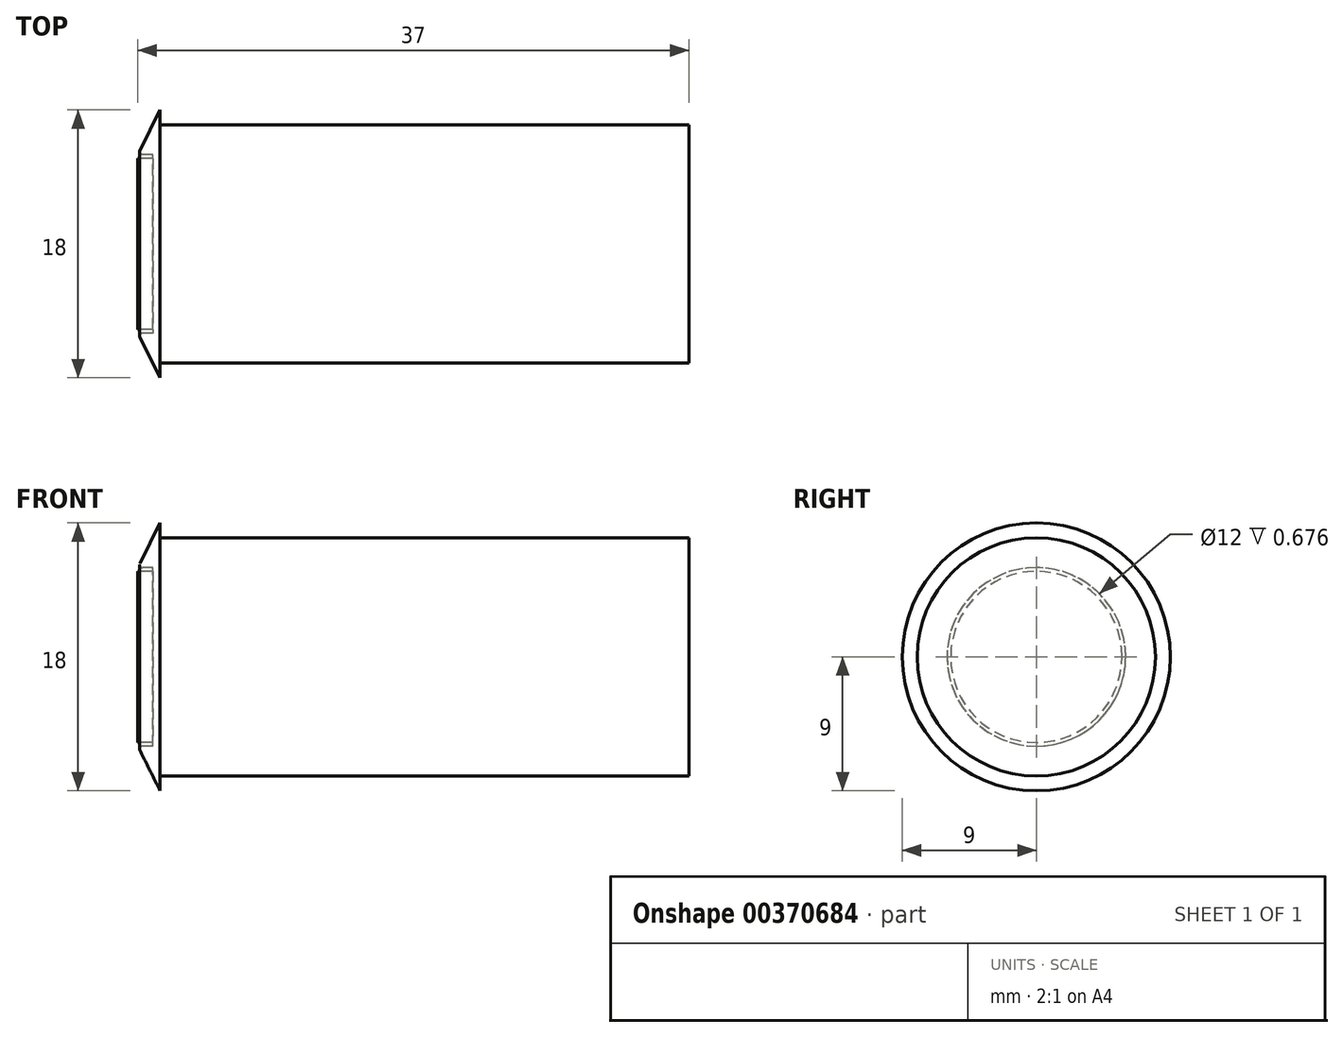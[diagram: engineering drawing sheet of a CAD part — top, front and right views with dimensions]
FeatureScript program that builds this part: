
annotation { "Feature Type Name" : "Feature", "Feature Type Description" : "" }
export const myFeature = defineFeature(function(context is Context, id is Id, definition is map)
    precondition{}
    {
        {
            var Q0;
            Q0=qCreatedBy(makeId("Front.planeOp"),FACE);
            var sketch = newSketch(context, id + "F0", { "sketchPlane" : qUnion([Q0])});
            skLineSegment(sketch, "E0", {"start": v(0, 0) * mm, "end": v(0, 6) * mm});
            skLineSegment(sketch, "E1", {"start": v(0, 6) * mm, "end": v(1.5, 9) * mm});
            skLineSegment(sketch, "E2", {"start": v(1.5, 9) * mm, "end": v(1.5, 8) * mm});
            skLineSegment(sketch, "E3", {"start": v(1.5, 8) * mm, "end": v(37, 8) * mm});
            skLineSegment(sketch, "E4", {"start": v(37, 8) * mm, "end": v(37, 0) * mm});
            skLineSegment(sketch, "E5", {"start": v(37, 0) * mm, "end": v(0, 0) * mm});
            skSolve(sketch);
        }
        {
            var Q0;
            Q0 = qSketchRegion(id + "F0", true);
            var Q1;
            Q1=sQuery(id+"F0.wireOp",EDGE,"E5");
            revolve(context, id + "F1", {"entities" : qUnion([Q0]), "axis" : qUnion([Q1]), "revolveType" : RevolveType.FULL});
        }
        {
            var Q0;
            Q0=makeQuery(id+"F1.opRevolve","SWEPT_FACE",FACE,{"disambiguationData":[OSD([sQuery(id+"F0.wireOp",EDGE,"E0")])]});
            var sketch = newSketch(context, id + "F2", { "sketchPlane" : qUnion([Q0])});
            skCircle(sketch, "E6", {"center": v(0, 0) * mm, "radius": 5.75 * mm});
            skCircle(sketch, "E7", {"center": v(0, 0) * mm, "radius": 6 * mm});
            skSolve(sketch);
        }
        {
            var Q0;
            Q0 = qSketchRegion(id + "F2", true);
            extrude(context, id + "F3", {"entities" : qUnion([Q0]), "operationType" : NewBodyOperationType.REMOVE, "oppositeDirection" : true, "depth" : 1 * mm});
        }
        {
            var Q0;
            Q0=makeQuery(id+"F3.boolean.opBoolean","MERGE",EDGE,{"derivedFrom":[makeQuery(id+"F1.opRevolve","SWEPT_EDGE",EDGE,{"disambiguationData":[OSD([sQuery(id+"F0.wireOp",EDGE,"E0"),sQuery(id+"F0.wireOp",EDGE,"E1")])]}),makeQuery(id+"F3.opExtrude","CAP_EDGE",EDGE,{"disambiguationData":[OSD([sQuery(id+"F2.wireOp",EDGE,"E7")])],"isStart":true})]});
            var Q1;
            Q1=makeQuery(id+"F3.boolean.opBoolean","COPY",EDGE,{"derivedFrom":makeQuery(id+"F3.opExtrude","CAP_EDGE",EDGE,{"disambiguationData":[OSD([sQuery(id+"F2.wireOp",EDGE,"E6")])],"isStart":true})});
            fillet(context, id + "F4", {"entities" : qUnion([Q0, Q1]), "radius" : 0.2 * mm, "tangentPropagation" : true, "allowEdgeOverflow" : false});
        }
    });
